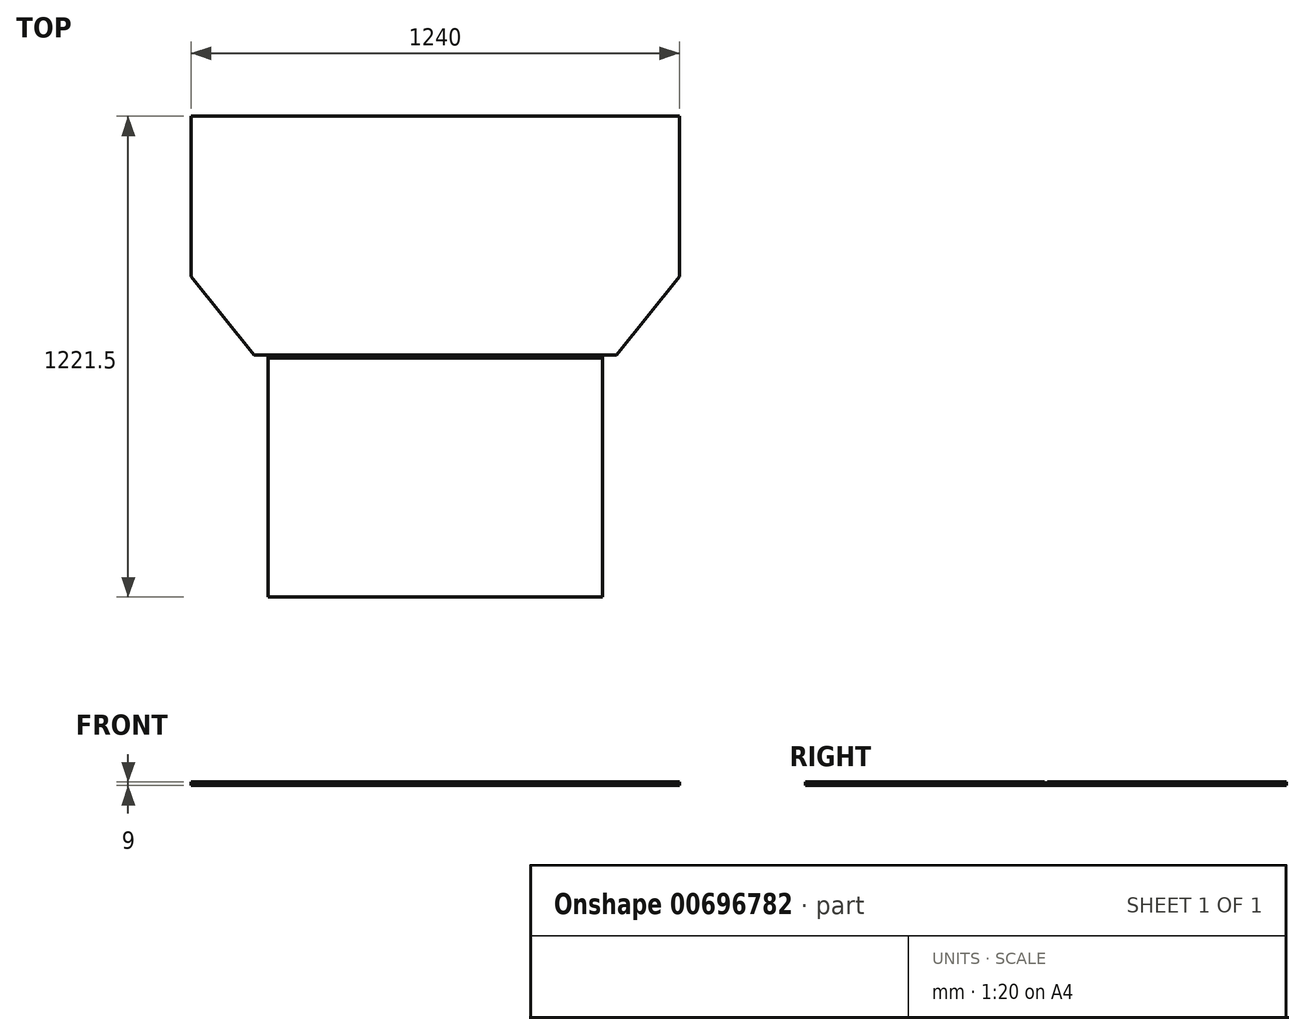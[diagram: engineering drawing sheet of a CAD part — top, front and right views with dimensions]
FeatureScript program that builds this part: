
annotation { "Feature Type Name" : "Feature", "Feature Type Description" : "" }
export const myFeature = defineFeature(function(context is Context, id is Id, definition is map)
    precondition{}
    {
        {
            var Q0;
            Q0=qCreatedBy(makeId("Top.planeOp"),FACE);
            var sketch = newSketch(context, id + "F0", { "sketchPlane" : qUnion([Q0])});
            skLineSegment(sketch, "E0.bottom", {"start": v(0, 0) * mm, "end": v(850, 0) * mm});
            skLineSegment(sketch, "E0.top", {"start": v(0, 607) * mm, "end": v(850, 607) * mm});
            skLineSegment(sketch, "E0.left", {"start": v(0, 0) * mm, "end": v(0, 607) * mm});
            skLineSegment(sketch, "E0.right", {"start": v(850, 0) * mm, "end": v(850, 607) * mm});
            skSolve(sketch);
        }
        {
            var Q0;
            Q0=makeQuery(id+"F0.imprint","IMPRINT",FACE,{"disambiguationData":[TD([[makeQuery(id+"F0.imprint","IMPRINT",EDGE,{"derivedFrom":sQuery(id+"F0.wireOp",EDGE,"E0.bottom")}),1.0]])]});
            extrude(context, id + "F1", {"entities" : qUnion([Q0]), "depth" : 9 * mm, "offsetDistance" : 25 * mm});
        }
        {
            var Q0;
            Q0=qCreatedBy(makeId("Top.planeOp"),FACE);
            var sketch = newSketch(context, id + "F2", { "sketchPlane" : qUnion([Q0])});
            skLineSegment(sketch, "E1.bottom", {"start": v(-195, 614.5) * mm, "end": v(1045, 614.5) * mm});
            skLineSegment(sketch, "E1.top", {"start": v(-195, 1221.5) * mm, "end": v(1045, 1221.5) * mm});
            skLineSegment(sketch, "E1.left", {"start": v(-195, 614.5) * mm, "end": v(-195, 1221.5) * mm});
            skLineSegment(sketch, "E1.right", {"start": v(1045, 614.5) * mm, "end": v(1045, 1221.5) * mm});
            skSolve(sketch);
        }
        {
            var Q0;
            Q0 = qSketchRegion(id + "F2", true);
            extrude(context, id + "F3", {"entities" : qUnion([Q0]), "depth" : 9 * mm, "offsetDistance" : 25 * mm});
        }
        {
            var Q0;
            Q0=makeQuery(id+"F3.opExtrude","CAP_FACE",FACE,{"disambiguationData":[OSD([sQuery(id+"F2.wireOp",EDGE,"E1.bottom"),sQuery(id+"F2.wireOp",EDGE,"E1.top"),sQuery(id+"F2.wireOp",EDGE,"E1.left"),sQuery(id+"F2.wireOp",EDGE,"E1.right")])],"isStart":false});
            var sketch = newSketch(context, id + "F4", { "sketchPlane" : qUnion([Q0])});
            skLineSegment(sketch, "E2", {"start": v(-195, 614.5) * mm, "end": v(-195, 814.5) * mm});
            skLineSegment(sketch, "E3", {"start": v(-195, 814.5) * mm, "end": v(-35, 614.5) * mm});
            skLineSegment(sketch, "E4", {"start": v(-35, 614.5) * mm, "end": v(-195, 614.5) * mm});
            skLineSegment(sketch, "E5", {"start": v(1045, 614.5) * mm, "end": v(1045, 814.5) * mm});
            skLineSegment(sketch, "E6", {"start": v(1045, 814.5) * mm, "end": v(885, 614.5) * mm});
            skLineSegment(sketch, "E7", {"start": v(885, 614.5) * mm, "end": v(1045, 614.5) * mm});
            skSolve(sketch);
        }
        {
            var Q0;
            Q0 = qSketchRegion(id + "F4", true);
            extrude(context, id + "F5", {"entities" : qUnion([Q0]), "operationType" : NewBodyOperationType.REMOVE, "oppositeDirection" : true, "depth" : 9 * mm, "offsetDistance" : 25 * mm});
        }
        {
            var Q0;
            Q0=makeQuery(id+"F1.opExtrude","SWEPT_FACE",FACE,{"disambiguationData":[OSD([sQuery(id+"F0.wireOp",EDGE,"E0.right")])]});
            var sketch = newSketch(context, id + "F6", { "sketchPlane" : qUnion([Q0])});
            skCircle(sketch, "E8", {"center": v(610.75, 3.75) * mm, "radius": 3.75 * mm});
            skSolve(sketch);
        }
        {
            var Q0;
            Q0 = qSketchRegion(id + "F6", true);
            extrude(context, id + "F7", {"entities" : qUnion([Q0]), "operationType" : NewBodyOperationType.ADD, "oppositeDirection" : true, "depth" : 50 * mm, "offsetDistance" : 25 * mm});
        }
        {
            var Q0;
            Q0=makeQuery(id+"F1.opExtrude","SWEPT_FACE",FACE,{"disambiguationData":[OSD([sQuery(id+"F0.wireOp",EDGE,"E0.right")])]});
            cPlane(context, id + "F8", {"entities" : qUnion([Q0]), "cplaneType" : CPlaneType.OFFSET, "offset" : 425 * mm, "oppositeDirection" : true, "width" : 150 * mm, "height" : 150 * mm});
        }
        {
            var Q0;
            Q0=makeQuery(id+"F7.opExtrude","SWEPT_BODY",BODY,{"disambiguationData":[OSD([sQuery(id+"F6.wireOp",EDGE,"E8")])]});
            var Q1;
            Q1=qCreatedBy(id+"F8.planeOp",FACE);
            mirror(context, id + "F9", {"entities" : qUnion([Q0]), "mirrorPlane" : qUnion([Q1])});
        }
    });
